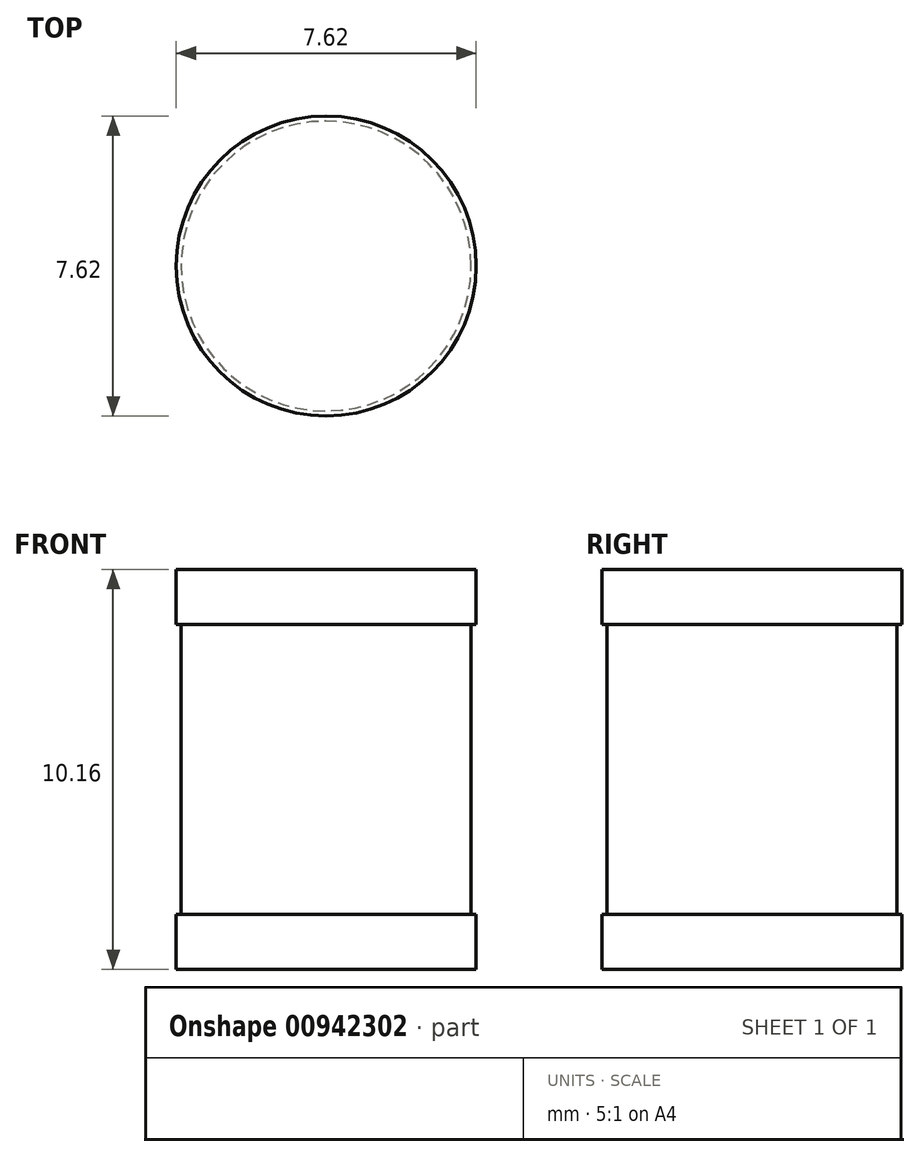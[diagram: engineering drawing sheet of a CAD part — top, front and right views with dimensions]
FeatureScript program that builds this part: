
annotation { "Feature Type Name" : "Feature", "Feature Type Description" : "" }
export const myFeature = defineFeature(function(context is Context, id is Id, definition is map)
    precondition{}
    {
        {
            var Q0;
            Q0=qCreatedBy(makeId("Top.planeOp"),FACE);
            var sketch = newSketch(context, id + "F0", { "sketchPlane" : qUnion([Q0])});
            skCircle(sketch, "E0", {"center": v(0, 0) * mm, "radius": 3.68 * mm});
            skCircle(sketch, "E1", {"center": v(0, 0) * mm, "radius": 3.81 * mm});
            skSolve(sketch);
        }
        {
            var Q0;
            Q0=makeQuery(id+"F0.imprint","IMPRINT",FACE,{"disambiguationData":[TD([[makeQuery(id+"F0.imprint","IMPRINT",EDGE,{"derivedFrom":sQuery(id+"F0.wireOp",EDGE,"E0")}),-1.0]])]});
            var Q1;
            Q1=makeQuery(id+"F0.imprint","IMPRINT",FACE,{"disambiguationData":[TD([[makeQuery(id+"F0.imprint","IMPRINT",EDGE,{"derivedFrom":sQuery(id+"F0.wireOp",EDGE,"E0")}),1.0]])]});
            extrude(context, id + "F1", {"entities" : qUnion([Q0, Q1]), "endBound" : BoundingType.SYMMETRIC, "depth" : 10.16 * mm, "offsetDistance" : 25.4 * mm});
        }
        {
            var Q0;
            Q0=makeQuery(id+"F0.imprint","IMPRINT",FACE,{"disambiguationData":[TD([[makeQuery(id+"F0.imprint","IMPRINT",EDGE,{"derivedFrom":sQuery(id+"F0.wireOp",EDGE,"E0")}),-1.0]])]});
            extrude(context, id + "F2", {"entities" : qUnion([Q0]), "operationType" : NewBodyOperationType.REMOVE, "endBound" : BoundingType.SYMMETRIC, "oppositeDirection" : true, "depth" : 7.37 * mm, "offsetDistance" : 25.4 * mm});
        }
    });
